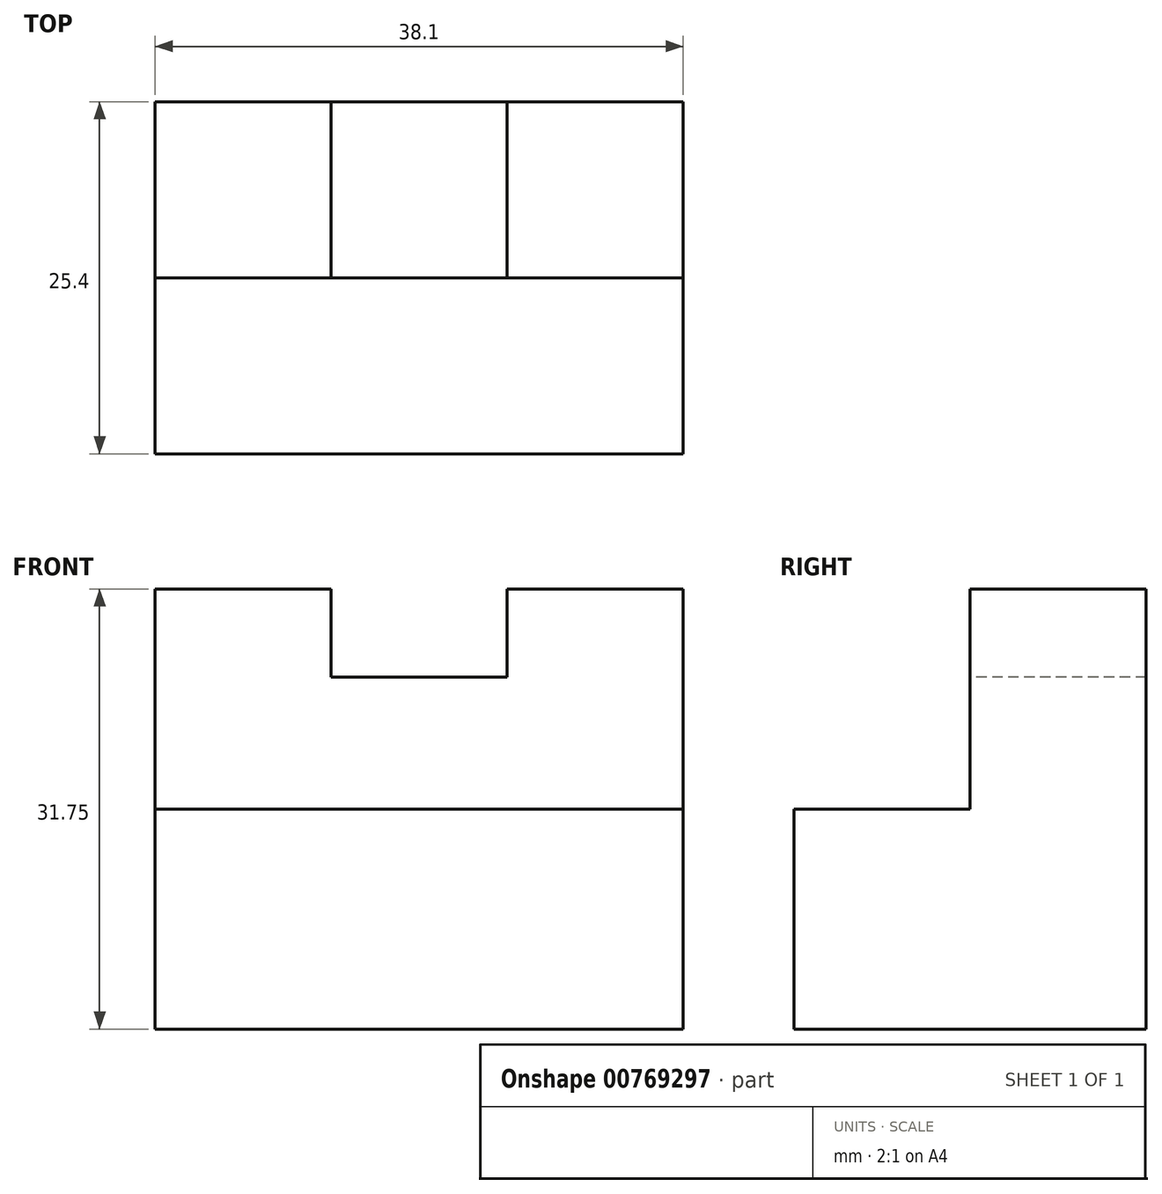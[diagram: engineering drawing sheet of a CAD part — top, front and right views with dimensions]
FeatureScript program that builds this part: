
annotation { "Feature Type Name" : "Feature", "Feature Type Description" : "" }
export const myFeature = defineFeature(function(context is Context, id is Id, definition is map)
    precondition{}
    {
        {
            var Q0;
            Q0=qCreatedBy(makeId("Front.planeOp"),FACE);
            var sketch = newSketch(context, id + "F0", { "sketchPlane" : qUnion([Q0])});
            skLineSegment(sketch, "E0", {"start": v(0, 0) * mm, "end": v(38.1, 0) * mm});
            skLineSegment(sketch, "E1", {"start": v(38.1, 0) * mm, "end": v(38.1, 31.75) * mm});
            skLineSegment(sketch, "E2", {"start": v(38.1, 31.75) * mm, "end": v(0, 31.75) * mm});
            skLineSegment(sketch, "E3", {"start": v(0, 31.75) * mm, "end": v(0, 0) * mm});
            skSolve(sketch);
        }
        {
            var Q0;
            Q0 = qSketchRegion(id + "F0", true);
            extrude(context, id + "F1", {"entities" : qUnion([Q0]), "depth" : 25.4 * mm, "offsetDistance" : 25.4 * mm});
        }
        {
            var Q0;
            Q0=makeQuery(id+"F1.opExtrude","CAP_FACE",FACE,{"disambiguationData":[OSD([sQuery(id+"F0.wireOp",EDGE,"E0"),sQuery(id+"F0.wireOp",EDGE,"E1"),sQuery(id+"F0.wireOp",EDGE,"E2"),sQuery(id+"F0.wireOp",EDGE,"E3")])],"isStart":false});
            var sketch = newSketch(context, id + "F2", { "sketchPlane" : qUnion([Q0])});
            skLineSegment(sketch, "E4", {"start": v(38.1, 31.75) * mm, "end": v(38.1, 15.88) * mm});
            skLineSegment(sketch, "E5", {"start": v(38.1, 15.88) * mm, "end": v(0, 15.88) * mm});
            skLineSegment(sketch, "E6", {"start": v(0, 15.88) * mm, "end": v(0, 31.75) * mm});
            skSolve(sketch);
        }
        {
            var Q0;
            Q0=makeQuery(id+"F2.imprint","IMPRINT",FACE,{"disambiguationData":[TD([[makeQuery(id+"F2.imprint","IMPRINT",EDGE,{"derivedFrom":sQuery(id+"F2.wireOp",EDGE,"E4")}),1.0]])]});
            extrude(context, id + "F3", {"entities" : qUnion([Q0]), "operationType" : NewBodyOperationType.REMOVE, "oppositeDirection" : true, "depth" : 12.7 * mm, "offsetDistance" : 25.4 * mm});
        }
        {
            var Q0;
            Q0=makeQuery(id+"F1.opExtrude","SWEPT_FACE",FACE,{"disambiguationData":[OSD([sQuery(id+"F0.wireOp",EDGE,"E2")])]});
            var sketch = newSketch(context, id + "F4", { "sketchPlane" : qUnion([Q0])});
            skLineSegment(sketch, "E7", {"start": v(12.7, 0) * mm, "end": v(12.7, -12.7) * mm});
            skLineSegment(sketch, "E8", {"start": v(12.7, -12.7) * mm, "end": v(25.4, -12.7) * mm});
            skLineSegment(sketch, "E9", {"start": v(25.4, -12.7) * mm, "end": v(25.4, 0) * mm});
            skSolve(sketch);
        }
        {
            var Q0;
            {var subQ0=sQuery(id+"F4.wireOp",EDGE,"E7");Q0=makeQuery(id+"F4.imprint","IMPRINT",FACE,{"disambiguationData":[TD([[makeQuery(id+"F4.imprint","IMPRINT",EDGE,{"derivedFrom":subQ0}),1.0]])]});}
            extrude(context, id + "F5", {"entities" : qUnion([Q0]), "operationType" : NewBodyOperationType.REMOVE, "oppositeDirection" : true, "depth" : 6.35 * mm, "offsetDistance" : 25.4 * mm});
        }
    });
